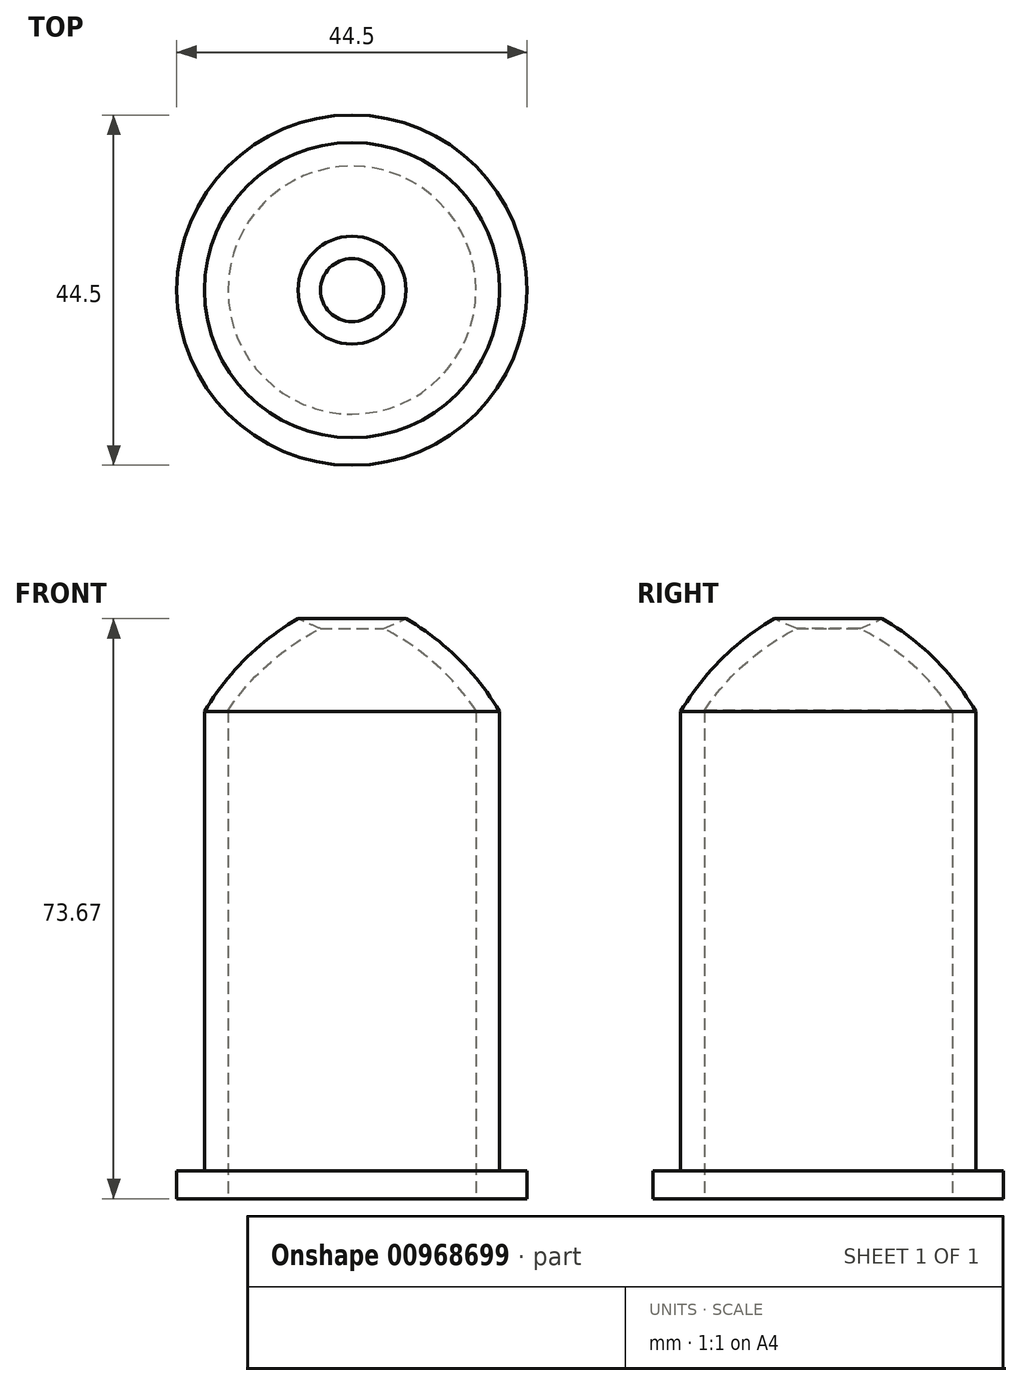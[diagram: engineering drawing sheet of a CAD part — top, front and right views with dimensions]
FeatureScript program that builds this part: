
annotation { "Feature Type Name" : "Feature", "Feature Type Description" : "" }
export const myFeature = defineFeature(function(context is Context, id is Id, definition is map)
    precondition{}
    {
        {
            var Q0;
            Q0=qCreatedBy(makeId("Front.planeOp"),FACE);
            var sketch = newSketch(context, id + "F0", { "sketchPlane" : qUnion([Q0])});
            skLineSegment(sketch, "E0", {"start": v(-15.75, 0) * mm, "end": v(-22.25, 0) * mm});
            skLineSegment(sketch, "E1", {"start": v(-22.25, 0) * mm, "end": v(-22.25, 3.5) * mm});
            skLineSegment(sketch, "E2", {"start": v(-22.25, 3.5) * mm, "end": v(-18.75, 3.5) * mm});
            skLineSegment(sketch, "E3", {"start": v(-18.75, 3.5) * mm, "end": v(-18.75, 61.86) * mm});
            skLineSegment(sketch, "E4", {"start": v(-15.75, 62) * mm, "end": v(-15.75, 0) * mm});
            skArc(sketch, "E5", {"start": v(-6.85, 73.66) * mm, "mid": v(-13.56, 68.52) * mm, "end": v(-18.75, 61.86) * mm});
            skPoint(sketch, "E5.second.point", {"position": v(0, 76.66) * mm});
            skPoint(sketch, "E5.third.point", {"position": v(32.66, 24.35) * mm});
            skArc(sketch, "E6", {"start": v(-4, 72.4) * mm, "mid": v(-10.55, 67.96) * mm, "end": v(-15.75, 62) * mm});
            skLineSegment(sketch, "E7", {"start": v(-4, 72.4) * mm, "end": v(-6.85, 73.66) * mm});
            skLineSegment(sketch, "E8", {"start": v(0, 0) * mm, "end": v(0, 86.48) * mm, "construction": true});
            skSolve(sketch);
        }
        {
            var Q0;
            Q0=makeQuery(id+"F0.imprint","IMPRINT",FACE,{"disambiguationData":[TD([[makeQuery(id+"F0.imprint","IMPRINT",EDGE,{"derivedFrom":sQuery(id+"F0.wireOp",EDGE,"E0")}),-1.0]])]});
            var Q1;
            Q1=sQuery(id+"F0.wireOp",EDGE,"E8");
            revolve(context, id + "F1", {"surfaceOperationType" : NewSurfaceOperationType.NEW, "entities" : qUnion([Q0]), "axis" : qUnion([Q1]), "revolveType" : RevolveType.FULL});
        }
    });
